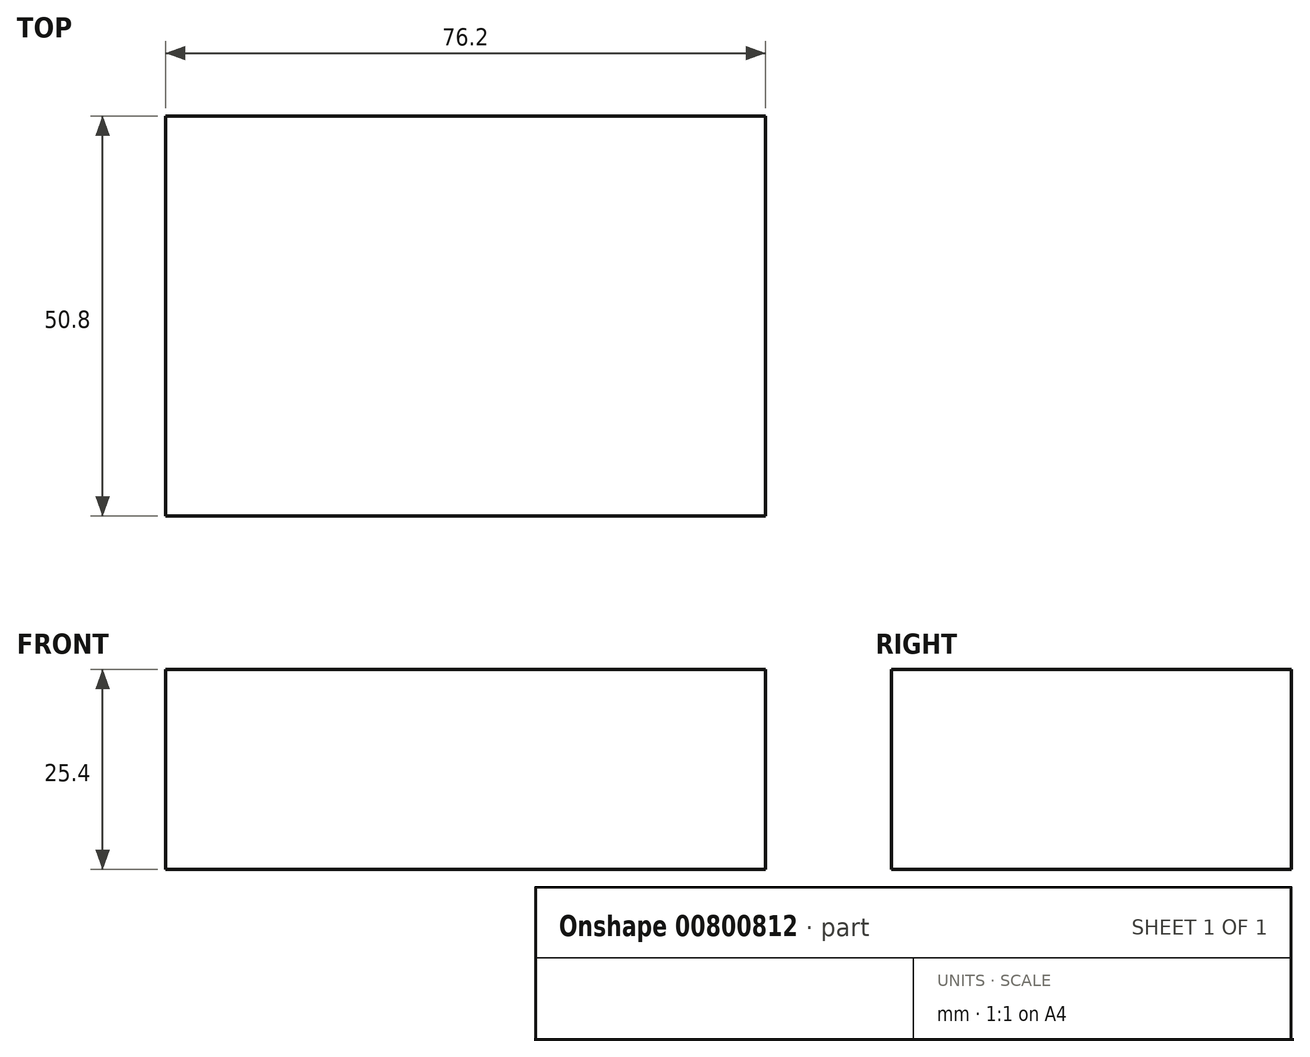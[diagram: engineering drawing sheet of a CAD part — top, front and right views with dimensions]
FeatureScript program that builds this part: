
annotation { "Feature Type Name" : "Feature", "Feature Type Description" : "" }
export const myFeature = defineFeature(function(context is Context, id is Id, definition is map)
    precondition{}
    {
        {
            var Q0;
            Q0=qCreatedBy(makeId("Top.planeOp"),FACE);
            var sketch = newSketch(context, id + "F0", { "sketchPlane" : qUnion([Q0])});
            skLineSegment(sketch, "E0.bottom", {"start": v(0, 0) * mm, "end": v(76.2, 0) * mm});
            skLineSegment(sketch, "E0.top", {"start": v(0, 50.8) * mm, "end": v(76.2, 50.8) * mm});
            skLineSegment(sketch, "E0.left", {"start": v(0, 0) * mm, "end": v(0, 50.8) * mm});
            skLineSegment(sketch, "E0.right", {"start": v(76.2, 0) * mm, "end": v(76.2, 50.8) * mm});
            skSolve(sketch);
        }
        {
            var Q0;
            Q0 = qSketchRegion(id + "F0", true);
            extrude(context, id + "F1", {"entities" : qUnion([Q0]), "depth" : 25.4 * mm, "offsetDistance" : 25.4 * mm});
        }
    });
